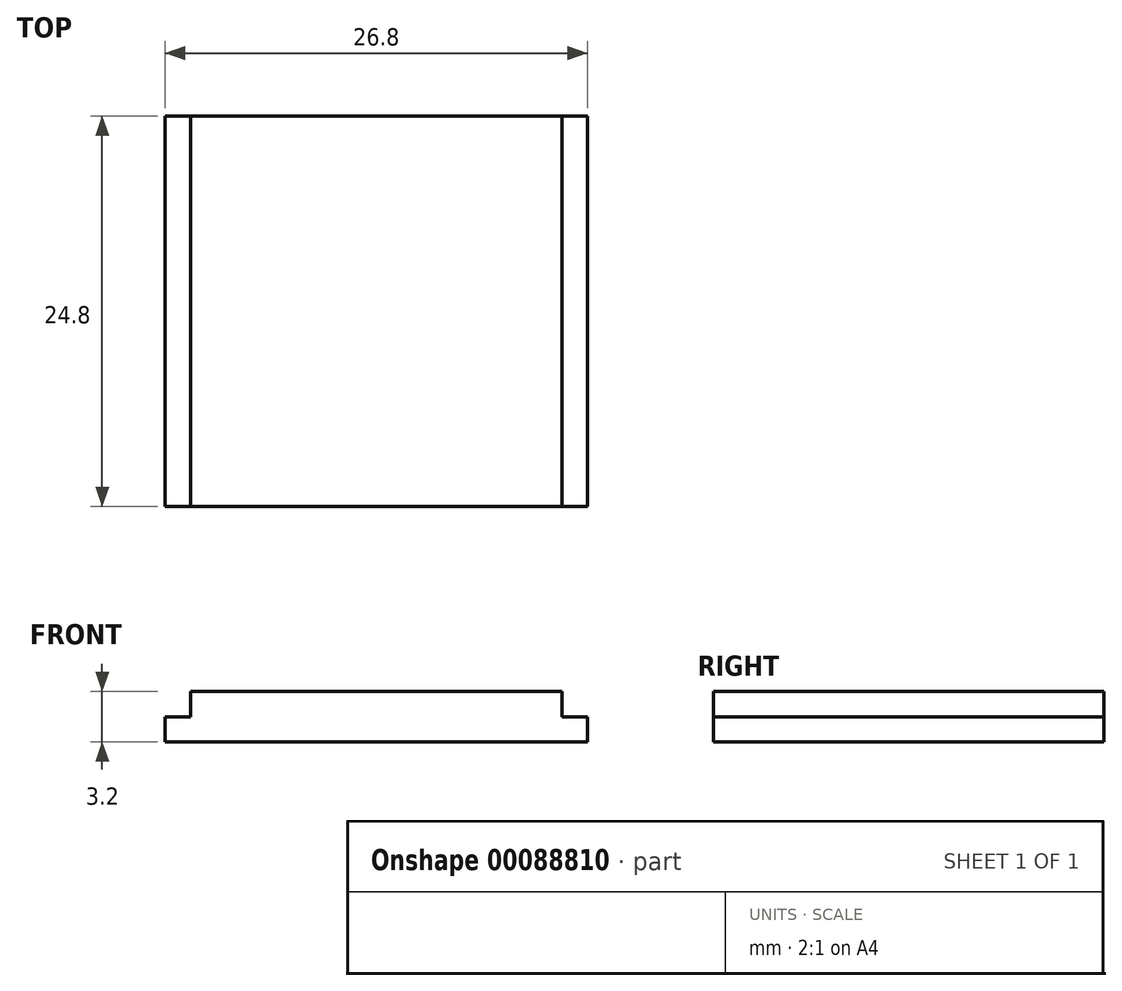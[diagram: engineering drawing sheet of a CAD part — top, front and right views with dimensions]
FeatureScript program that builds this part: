
annotation { "Feature Type Name" : "Feature", "Feature Type Description" : "" }
export const myFeature = defineFeature(function(context is Context, id is Id, definition is map)
    precondition{}
    {
        {
            var Q0;
            Q0=qCreatedBy(makeId("Front.planeOp"),FACE);
            var sketch = newSketch(context, id + "F0", { "sketchPlane" : qUnion([Q0])});
            skLineSegment(sketch, "E0", {"start": v(0, 0) * mm, "end": v(-13.4, 0) * mm});
            skLineSegment(sketch, "E1", {"start": v(-13.4, 0) * mm, "end": v(-13.4, 1.6) * mm});
            skLineSegment(sketch, "E2", {"start": v(-13.4, 1.6) * mm, "end": v(-11.8, 1.6) * mm});
            skLineSegment(sketch, "E3", {"start": v(-11.8, 1.6) * mm, "end": v(-11.8, 3.2) * mm});
            skLineSegment(sketch, "E4", {"start": v(-11.8, 3.2) * mm, "end": v(0, 3.2) * mm});
            skLineSegment(sketch, "E5", {"start": v(0, 0) * mm, "end": v(0, 3.2) * mm, "construction": true});
            skLineSegment(sketch, "E6.MirrorCS", {"start": v(11.8, 3.2) * mm, "end": v(0, 3.2) * mm});
            skLineSegment(sketch, "E7.MirrorCS", {"start": v(11.8, 1.6) * mm, "end": v(11.8, 3.2) * mm});
            skLineSegment(sketch, "E8.MirrorCS", {"start": v(13.4, 1.6) * mm, "end": v(11.8, 1.6) * mm});
            skLineSegment(sketch, "E9.MirrorCS", {"start": v(13.4, 0) * mm, "end": v(13.4, 1.6) * mm});
            skLineSegment(sketch, "E10.MirrorCS", {"start": v(0, 0) * mm, "end": v(13.4, 0) * mm});
            skSolve(sketch);
        }
        {
            var Q0;
            Q0=makeQuery(id+"F0.imprint","IMPRINT",FACE,{"disambiguationData":[TD([[makeQuery(id+"F0.imprint","IMPRINT",EDGE,{"derivedFrom":sQuery(id+"F0.wireOp",EDGE,"E0")}),-1.0]])]});
            extrude(context, id + "F1", {"entities" : qUnion([Q0]), "depth" : 24.8 * mm});
        }
    });
